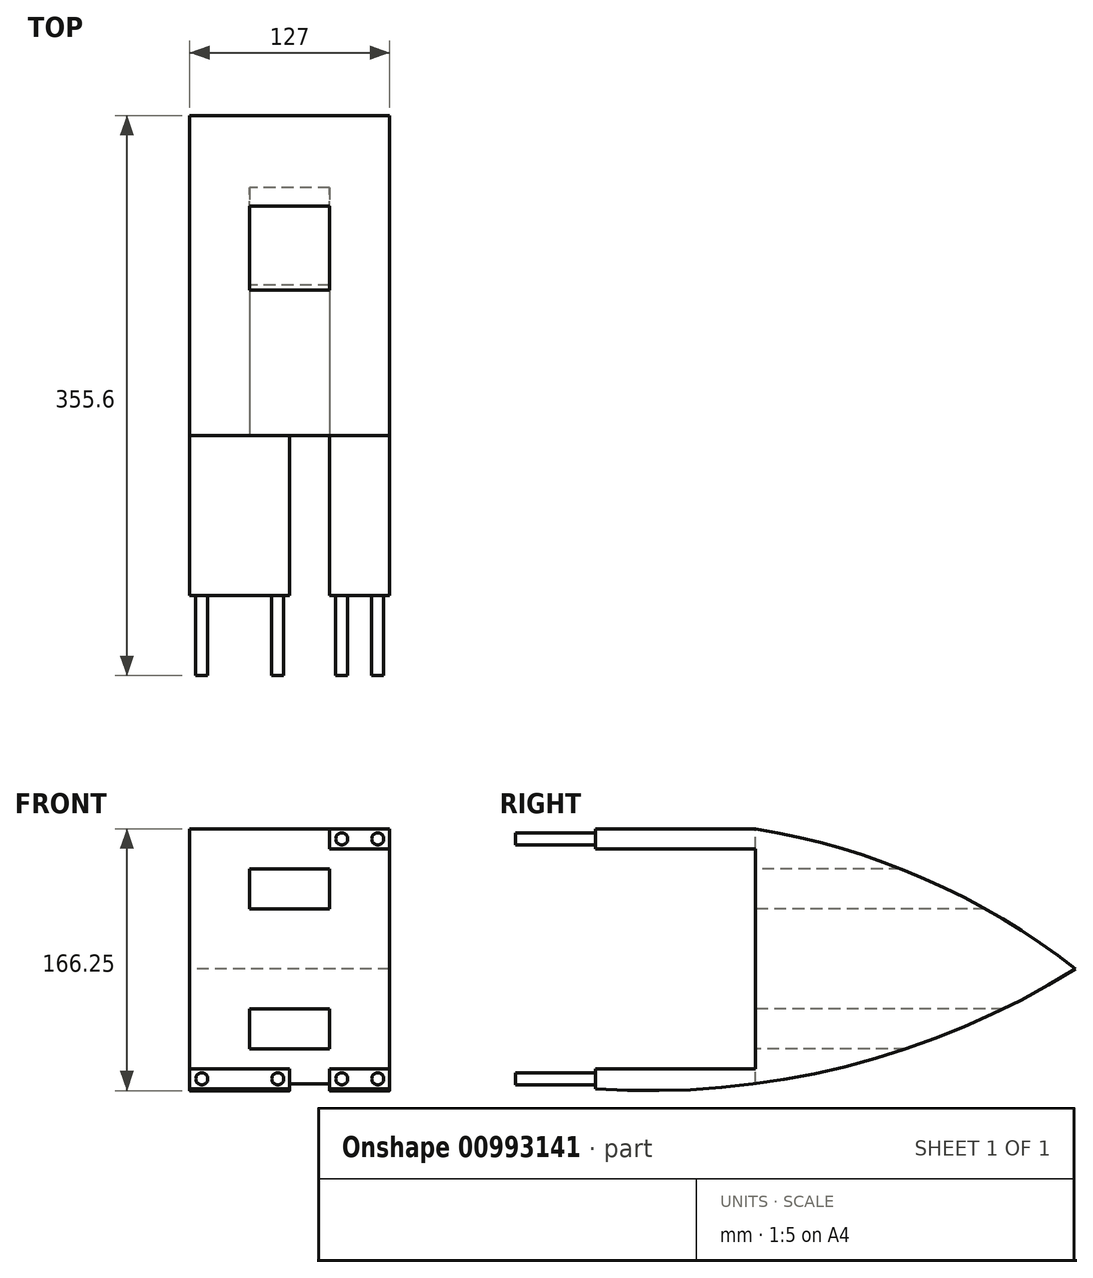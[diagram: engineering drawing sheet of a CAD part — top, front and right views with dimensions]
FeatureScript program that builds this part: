
annotation { "Feature Type Name" : "Feature", "Feature Type Description" : "" }
export const myFeature = defineFeature(function(context is Context, id is Id, definition is map)
    precondition{}
    {
        {
            var Q0;
            Q0=qCreatedBy(makeId("Right.planeOp"),FACE);
            var sketch = newSketch(context, id + "F0", { "sketchPlane" : qUnion([Q0])});
            skLineSegment(sketch, "E0", {"start": v(-50.03, 29.01) * mm, "end": v(153.17, 29.01) * mm});
            skLineSegment(sketch, "E1", {"start": v(-50.03, 29.01) * mm, "end": v(-50.03, 117.91) * mm});
            skLineSegment(sketch, "E2", {"start": v(-50.03, 29.01) * mm, "end": v(-50.03, -34.49) * mm});
            skLineSegment(sketch, "E3", {"start": v(-50.03, -34.49) * mm, "end": v(-151.63, -34.49) * mm});
            skLineSegment(sketch, "E4", {"start": v(-151.63, -34.49) * mm, "end": v(-151.63, -47.19) * mm});
            skArc(sketch, "E5", {"start": v(-151.63, -47.19) * mm, "mid": v(6.77, -33.08) * mm, "end": v(153.17, 29.01) * mm});
            skArc(sketch, "E6", {"start": v(153.17, 29.01) * mm, "mid": v(57.18, 86.27) * mm, "end": v(-50.03, 117.91) * mm});
            skSolve(sketch);
        }
        {
            var Q0;
            Q0=makeQuery(id+"F0.imprint","IMPRINT",FACE,{"disambiguationData":[TD([[makeQuery(id+"F0.imprint","IMPRINT",EDGE,{"derivedFrom":sQuery(id+"F0.wireOp",EDGE,"E0")}),1.0]])]});
            var Q1;
            Q1=makeQuery(id+"F0.imprint","IMPRINT",FACE,{"disambiguationData":[TD([[makeQuery(id+"F0.imprint","IMPRINT",EDGE,{"derivedFrom":sQuery(id+"F0.wireOp",EDGE,"E0")}),-1.0]])]});
            extrude(context, id + "F1", {"entities" : qUnion([Q0, Q1]), "depth" : 127 * mm, "offsetDistance" : 25.4 * mm});
        }
        {
            var Q0;
            Q0=makeQuery(id+"F1.opExtrude","SWEPT_FACE",FACE,{"disambiguationData":[OSD([sQuery(id+"F0.wireOp",EDGE,"E3")])]});
            var sketch = newSketch(context, id + "F2", { "sketchPlane" : qUnion([Q0])});
            skLineSegment(sketch, "E7.bottom", {"start": v(63.5, -151.63) * mm, "end": v(88.9, -151.63) * mm});
            skLineSegment(sketch, "E7.top", {"start": v(63.5, -50.03) * mm, "end": v(88.9, -50.03) * mm});
            skLineSegment(sketch, "E7.left", {"start": v(63.5, -151.63) * mm, "end": v(63.5, -50.03) * mm});
            skLineSegment(sketch, "E7.right", {"start": v(88.9, -151.63) * mm, "end": v(88.9, -50.03) * mm});
            skSolve(sketch);
        }
        {
            var Q0;
            Q0=makeQuery(id+"F2.imprint","IMPRINT",FACE,{"disambiguationData":[TD([[makeQuery(id+"F2.imprint","IMPRINT",EDGE,{"derivedFrom":sQuery(id+"F2.wireOp",EDGE,"E7.bottom")}),-1.0]])]});
            extrude(context, id + "F3", {"entities" : qUnion([Q0]), "operationType" : NewBodyOperationType.REMOVE, "oppositeDirection" : true, "depth" : 25.4 * mm, "offsetDistance" : 25.4 * mm});
        }
        {
            var Q0;
            Q0=makeQuery(id+"F3.boolean.opBoolean","MERGE",FACE,{"derivedFrom":[makeQuery(id+"F1.opExtrude","SWEPT_FACE",FACE,{"disambiguationData":[OSD([sQuery(id+"F0.wireOp",EDGE,"E1"),sQuery(id+"F0.wireOp",EDGE,"E2")])]})],"fromTools":[makeQuery(id+"F3.opExtrude","SWEPT_FACE",FACE,{"disambiguationData":[OSD([sQuery(id+"F2.wireOp",EDGE,"E7.top")])]})]});
            var sketch = newSketch(context, id + "F4", { "sketchPlane" : qUnion([Q0])});
            skLineSegment(sketch, "E8.bottom", {"start": v(88.9, 92.51) * mm, "end": v(38.1, 92.51) * mm});
            skLineSegment(sketch, "E8.top", {"start": v(88.9, 67.11) * mm, "end": v(38.1, 67.11) * mm});
            skLineSegment(sketch, "E8.left", {"start": v(88.9, 92.51) * mm, "end": v(88.9, 67.11) * mm});
            skLineSegment(sketch, "E8.right", {"start": v(38.1, 92.51) * mm, "end": v(38.1, 67.11) * mm});
            skPoint(sketch, "E8.middle", {"position": v(63.5, 79.81) * mm});
            skPoint(sketch, "E8.middle.positionSnap0", {"position": v(63.5, 117.91) * mm});
            skPoint(sketch, "E8.centerSnap0", {"position": v(63.5, 117.91) * mm});
            skLineSegment(sketch, "E9.bottom", {"start": v(88.9, -21.79) * mm, "end": v(38.1, -21.79) * mm});
            skLineSegment(sketch, "E9.top", {"start": v(88.9, 3.61) * mm, "end": v(38.1, 3.61) * mm});
            skLineSegment(sketch, "E9.left", {"start": v(88.9, -21.79) * mm, "end": v(88.9, 3.61) * mm});
            skLineSegment(sketch, "E9.right", {"start": v(38.1, -21.79) * mm, "end": v(38.1, 3.61) * mm});
            skPoint(sketch, "E9.middle", {"position": v(63.5, -9.09) * mm});
            skSolve(sketch);
        }
        {
            var Q0;
            Q0=makeQuery(id+"F4.imprint","IMPRINT",FACE,{"disambiguationData":[TD([[makeQuery(id+"F4.imprint","IMPRINT",EDGE,{"derivedFrom":sQuery(id+"F4.wireOp",EDGE,"E8.bottom")}),1.0]])]});
            var Q1;
            Q1=makeQuery(id+"F4.imprint","IMPRINT",FACE,{"disambiguationData":[TD([[makeQuery(id+"F4.imprint","IMPRINT",EDGE,{"derivedFrom":sQuery(id+"F4.wireOp",EDGE,"E9.bottom")}),-1.0]])]});
            extrude(context, id + "F5", {"entities" : qUnion([Q0, Q1]), "operationType" : NewBodyOperationType.REMOVE, "oppositeDirection" : true, "depth" : 203.2 * mm, "offsetDistance" : 25.4 * mm});
        }
        {
            var Q0;
            {var subQ1=sQuery(id+"F0.wireOp",EDGE,"E4");Q0=makeQuery(id+"F3.boolean.opBoolean","SPLIT",FACE,{"disambiguationData":[TD([makeQuery(id+"F3.opExtrude","SWEPT_FACE",FACE,{"disambiguationData":[OSD([sQuery(id+"F2.wireOp",EDGE,"E7.right")])]})])],"derivedFrom":makeQuery(id+"F1.opExtrude","SWEPT_FACE",FACE,{"disambiguationData":[OSD([subQ1])]})});}
            var sketch = newSketch(context, id + "F6", { "sketchPlane" : qUnion([Q0])});
            skCircle(sketch, "E10", {"center": v(119.38, -40.84) * mm, "radius": 3.81 * mm});
            skPoint(sketch, "E10.centerSnap0", {"position": v(127, -40.84) * mm});
            skCircle(sketch, "E11", {"center": v(96.52, -40.84) * mm, "radius": 3.81 * mm});
            skPoint(sketch, "E11.centerSnap0", {"position": v(88.9, -40.84) * mm});
            skSolve(sketch);
        }
        {
            var Q0;
            Q0=makeQuery(id+"F6.imprint","IMPRINT",FACE,{"disambiguationData":[TD([[makeQuery(id+"F6.imprint","IMPRINT",EDGE,{"derivedFrom":sQuery(id+"F6.wireOp",EDGE,"E11")}),1.0]])]});
            var Q1;
            Q1=makeQuery(id+"F6.imprint","IMPRINT",FACE,{"disambiguationData":[TD([[makeQuery(id+"F6.imprint","IMPRINT",EDGE,{"derivedFrom":sQuery(id+"F6.wireOp",EDGE,"E10")}),1.0]])]});
            extrude(context, id + "F7", {"entities" : qUnion([Q0, Q1]), "operationType" : NewBodyOperationType.ADD, "depth" : 50.8 * mm, "offsetDistance" : 25.4 * mm});
        }
        {
            var Q0;
            {var subQ1=sQuery(id+"F0.wireOp",EDGE,"E4");Q0=makeQuery(id+"F3.boolean.opBoolean","SPLIT",FACE,{"disambiguationData":[TD([makeQuery(id+"F3.opExtrude","SWEPT_FACE",FACE,{"disambiguationData":[OSD([sQuery(id+"F2.wireOp",EDGE,"E7.left")])]})])],"derivedFrom":makeQuery(id+"F1.opExtrude","SWEPT_FACE",FACE,{"disambiguationData":[OSD([subQ1])]})});}
            var sketch = newSketch(context, id + "F8", { "sketchPlane" : qUnion([Q0])});
            skCircle(sketch, "E12", {"center": v(7.62, -40.84) * mm, "radius": 3.81 * mm});
            skPoint(sketch, "E12.centerSnap0", {"position": v(0, -40.84) * mm});
            skCircle(sketch, "E13", {"center": v(55.88, -40.84) * mm, "radius": 3.81 * mm});
            skPoint(sketch, "E13.centerSnap0", {"position": v(63.5, -40.84) * mm});
            skSolve(sketch);
        }
        {
            var Q0;
            Q0=makeQuery(id+"F8.imprint","IMPRINT",FACE,{"disambiguationData":[TD([[makeQuery(id+"F8.imprint","IMPRINT",EDGE,{"derivedFrom":sQuery(id+"F8.wireOp",EDGE,"E12")}),1.0]])]});
            var Q1;
            Q1=makeQuery(id+"F8.imprint","IMPRINT",FACE,{"disambiguationData":[TD([[makeQuery(id+"F8.imprint","IMPRINT",EDGE,{"derivedFrom":sQuery(id+"F8.wireOp",EDGE,"E13")}),1.0]])]});
            extrude(context, id + "F9", {"entities" : qUnion([Q0, Q1]), "operationType" : NewBodyOperationType.ADD, "depth" : 50.8 * mm, "offsetDistance" : 25.4 * mm});
        }
        {
            var Q0;
            Q0=makeQuery(id+"F3.boolean.opBoolean","MERGE",FACE,{"derivedFrom":[makeQuery(id+"F1.opExtrude","SWEPT_FACE",FACE,{"disambiguationData":[OSD([sQuery(id+"F0.wireOp",EDGE,"E1"),sQuery(id+"F0.wireOp",EDGE,"E2")])]})],"fromTools":[makeQuery(id+"F3.opExtrude","SWEPT_FACE",FACE,{"disambiguationData":[OSD([sQuery(id+"F2.wireOp",EDGE,"E7.top")])]})]});
            var sketch = newSketch(context, id + "F10", { "sketchPlane" : qUnion([Q0])});
            skLineSegment(sketch, "E14.bottom", {"start": v(88.9, 105.21) * mm, "end": v(127, 105.21) * mm});
            skLineSegment(sketch, "E14.top", {"start": v(88.9, 117.91) * mm, "end": v(127, 117.91) * mm});
            skLineSegment(sketch, "E14.left", {"start": v(88.9, 105.21) * mm, "end": v(88.9, 117.91) * mm});
            skLineSegment(sketch, "E14.right", {"start": v(127, 105.21) * mm, "end": v(127, 117.91) * mm});
            skSolve(sketch);
        }
        {
            var Q0;
            Q0=makeQuery(id+"F10.imprint","IMPRINT",FACE,{"disambiguationData":[TD([[makeQuery(id+"F10.imprint","IMPRINT",EDGE,{"derivedFrom":sQuery(id+"F10.wireOp",EDGE,"E14.bottom")}),1.0]])]});
            extrude(context, id + "F11", {"entities" : qUnion([Q0]), "operationType" : NewBodyOperationType.ADD, "depth" : 101.6 * mm, "offsetDistance" : 25.4 * mm});
        }
        {
            var Q0;
            Q0=makeQuery(id+"F11.opExtrude","CAP_FACE",FACE,{"disambiguationData":[OSD([sQuery(id+"F10.wireOp",EDGE,"E14.bottom"),sQuery(id+"F10.wireOp",EDGE,"E14.top"),sQuery(id+"F10.wireOp",EDGE,"E14.left"),sQuery(id+"F10.wireOp",EDGE,"E14.right")])],"isStart":false});
            var sketch = newSketch(context, id + "F12", { "sketchPlane" : qUnion([Q0])});
            skCircle(sketch, "E15", {"center": v(119.38, 111.56) * mm, "radius": 3.81 * mm});
            skPoint(sketch, "E15.centerSnap0", {"position": v(127, 111.56) * mm});
            skCircle(sketch, "E16", {"center": v(96.52, 111.56) * mm, "radius": 3.81 * mm});
            skPoint(sketch, "E16.centerSnap0", {"position": v(88.9, 111.56) * mm});
            skSolve(sketch);
        }
        {
            var Q0;
            Q0=makeQuery(id+"F12.imprint","IMPRINT",FACE,{"disambiguationData":[TD([[makeQuery(id+"F12.imprint","IMPRINT",EDGE,{"derivedFrom":sQuery(id+"F12.wireOp",EDGE,"E16")}),1.0]])]});
            var Q1;
            Q1=makeQuery(id+"F12.imprint","IMPRINT",FACE,{"disambiguationData":[TD([[makeQuery(id+"F12.imprint","IMPRINT",EDGE,{"derivedFrom":sQuery(id+"F12.wireOp",EDGE,"E15")}),1.0]])]});
            extrude(context, id + "F13", {"entities" : qUnion([Q0, Q1]), "operationType" : NewBodyOperationType.ADD, "depth" : 50.8 * mm, "offsetDistance" : 25.4 * mm});
        }
    });
